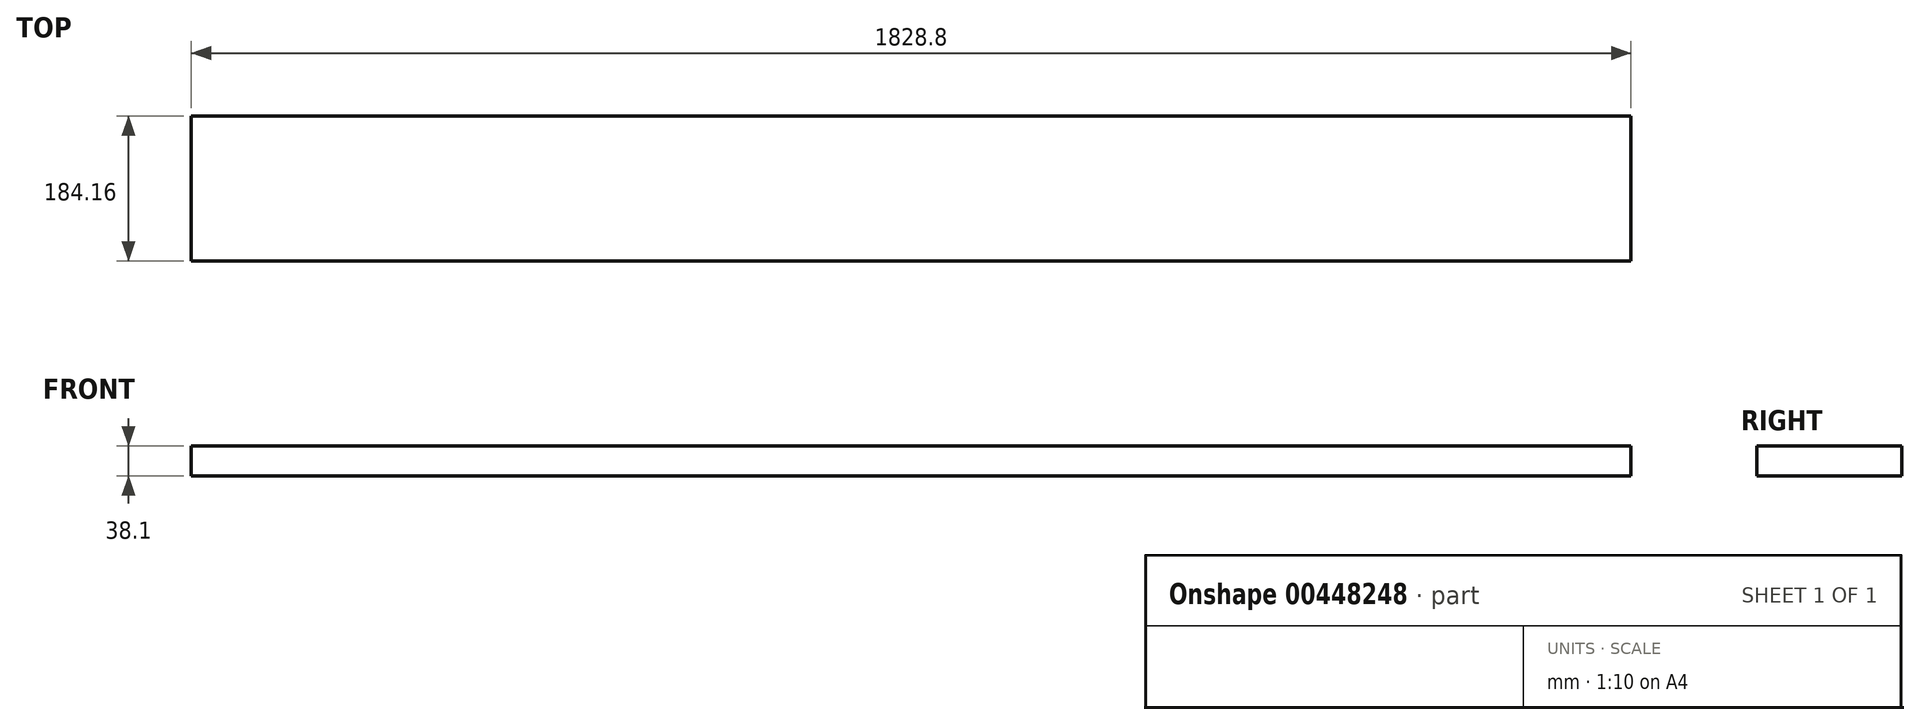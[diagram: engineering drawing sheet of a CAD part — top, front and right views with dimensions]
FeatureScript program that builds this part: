
annotation { "Feature Type Name" : "Feature", "Feature Type Description" : "" }
export const myFeature = defineFeature(function(context is Context, id is Id, definition is map)
    precondition{}
    {
        {
            var Q0;
            Q0=qCreatedBy(makeId("Top.planeOp"),FACE);
            var sketch = newSketch(context, id + "F0", { "sketchPlane" : qUnion([Q0])});
            skLineSegment(sketch, "E0.bottom", {"start": v(-914.4, 92.08) * mm, "end": v(914.4, 92.07) * mm});
            skLineSegment(sketch, "E0.top", {"start": v(-914.4, -92.07) * mm, "end": v(914.4, -92.08) * mm});
            skLineSegment(sketch, "E0.left", {"start": v(-914.4, 92.07) * mm, "end": v(-914.4, -92.07) * mm});
            skLineSegment(sketch, "E0.right", {"start": v(914.4, 92.07) * mm, "end": v(914.4, -92.07) * mm});
            skSolve(sketch);
        }
        {
            var Q0;
            Q0=makeQuery(id+"F0.imprint","IMPRINT",FACE,{"disambiguationData":[TD([[makeQuery(id+"F0.imprint","IMPRINT",EDGE,{"derivedFrom":sQuery(id+"F0.wireOp",EDGE,"E0.bottom")}),-1.0]])]});
            extrude(context, id + "F1", {"entities" : qUnion([Q0]), "depth" : 38.1 * mm});
        }
    });
